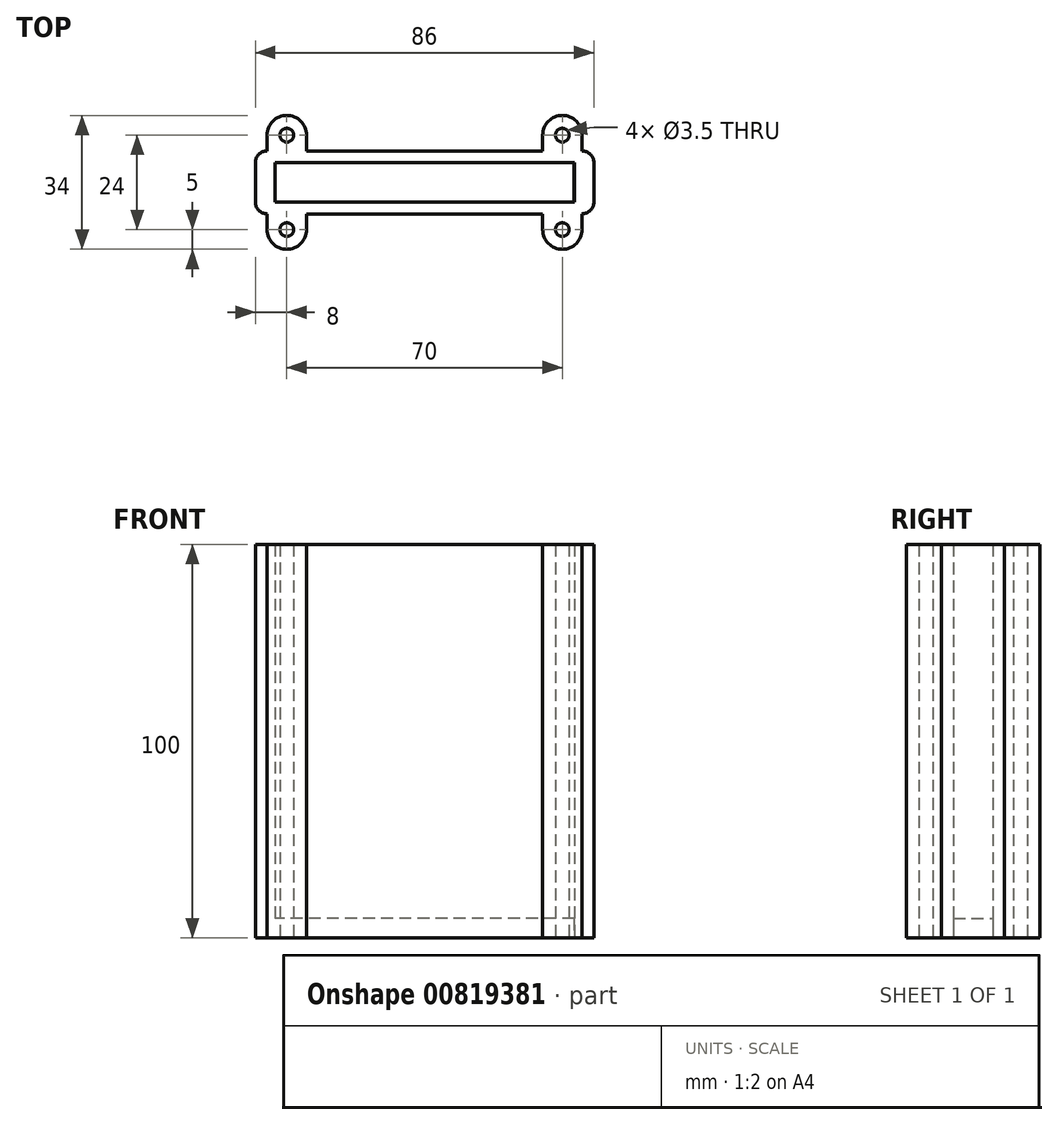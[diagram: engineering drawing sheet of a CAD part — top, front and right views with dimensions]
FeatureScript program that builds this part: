
annotation { "Feature Type Name" : "Feature", "Feature Type Description" : "" }
export const myFeature = defineFeature(function(context is Context, id is Id, definition is map)
    precondition{}
    {
        {
            var Q0;
            Q0=qCreatedBy(makeId("Top.planeOp"),FACE);
            var sketch = newSketch(context, id + "F0", { "sketchPlane" : qUnion([Q0])});
            skLineSegment(sketch, "E0.bottom", {"start": v(38.09, -5) * mm, "end": v(-37.94, -5) * mm});
            skLineSegment(sketch, "E0.top", {"start": v(38.09, 5) * mm, "end": v(-37.94, 5) * mm});
            skPoint(sketch, "E0.middle", {"position": v(0, 0) * mm});
            skLineSegment(sketch, "E1.0", {"start": v(40, 8) * mm, "end": v(-40, 8) * mm});
            skLineSegment(sketch, "E1.1", {"start": v(43, -5) * mm, "end": v(43, 5) * mm});
            skLineSegment(sketch, "E1.2", {"start": v(40, -8) * mm, "end": v(-40, -8) * mm});
            skLineSegment(sketch, "E1.3", {"start": v(-43, -5) * mm, "end": v(-43, 5) * mm});
            skPoint(sketch, "E2.visualSharp", {"position": v(-43, 8) * mm});
            skArc(sketch, "E2.filletArc", {"start": v(-40, 8) * mm, "mid": v(-42.12, 7.12) * mm, "end": v(-43, 5) * mm});
            skPoint(sketch, "E3.visualSharp", {"position": v(-43, -8) * mm});
            skArc(sketch, "E3.filletArc", {"start": v(-43, -5) * mm, "mid": v(-42.12, -7.12) * mm, "end": v(-40, -8) * mm});
            skPoint(sketch, "E4.visualSharp", {"position": v(43, 8) * mm});
            skArc(sketch, "E4.filletArc", {"start": v(43, 5) * mm, "mid": v(42.12, 7.12) * mm, "end": v(40, 8) * mm});
            skPoint(sketch, "E5.visualSharp", {"position": v(43, -8) * mm});
            skArc(sketch, "E5.filletArc", {"start": v(40, -8) * mm, "mid": v(42.12, -7.12) * mm, "end": v(43, -5) * mm});
            skLineSegment(sketch, "E6", {"start": v(40, -8) * mm, "end": v(40, -12) * mm});
            skLineSegment(sketch, "E7", {"start": v(-40, 8) * mm, "end": v(-40, 12) * mm});
            skLineSegment(sketch, "E8", {"start": v(-30, 12) * mm, "end": v(-40, 12) * mm});
            skLineSegment(sketch, "E9", {"start": v(-30, 12) * mm, "end": v(-30, 8) * mm});
            skLineSegment(sketch, "E10", {"start": v(40, 8) * mm, "end": v(40, 12) * mm});
            skLineSegment(sketch, "E11", {"start": v(40, 12) * mm, "end": v(30, 12) * mm});
            skLineSegment(sketch, "E12", {"start": v(30, 12) * mm, "end": v(30, 8) * mm});
            skArc(sketch, "E13", {"start": v(-30, 12) * mm, "mid": v(-35, 17) * mm, "end": v(-40, 12) * mm});
            skArc(sketch, "E14", {"start": v(40, 12) * mm, "mid": v(35, 17) * mm, "end": v(30, 12) * mm});
            skCircle(sketch, "E15", {"center": v(-35, 12) * mm, "radius": 1.75 * mm});
            skCircle(sketch, "E16", {"center": v(35, 12) * mm, "radius": 1.75 * mm});
            skLineSegment(sketch, "E17", {"start": v(40, -12) * mm, "end": v(30, -12) * mm});
            skLineSegment(sketch, "E18", {"start": v(30, -12) * mm, "end": v(30, -8) * mm});
            skLineSegment(sketch, "E19", {"start": v(-40, -8) * mm, "end": v(-40, -12) * mm});
            skLineSegment(sketch, "E20", {"start": v(-30, -12) * mm, "end": v(-40, -12) * mm});
            skLineSegment(sketch, "E21", {"start": v(-30, -12) * mm, "end": v(-30, -8) * mm});
            skArc(sketch, "E22", {"start": v(30, -12) * mm, "mid": v(35, -17) * mm, "end": v(40, -12) * mm});
            skArc(sketch, "E23", {"start": v(-40, -12) * mm, "mid": v(-35, -17) * mm, "end": v(-30, -12) * mm});
            skCircle(sketch, "E24", {"center": v(-35, -12) * mm, "radius": 1.75 * mm});
            skCircle(sketch, "E25", {"center": v(35, -12) * mm, "radius": 1.75 * mm});
            skLineSegment(sketch, "E26", {"start": v(-37.94, 5) * mm, "end": v(-37.94, -5) * mm});
            skLineSegment(sketch, "E27", {"start": v(38.09, 5) * mm, "end": v(38.09, -5) * mm});
            skSolve(sketch);
        }
        {
            var Q0;
            Q0=qCreatedBy(makeId("Top.planeOp"),FACE);
            var sketch = newSketch(context, id + "F1", { "sketchPlane" : qUnion([Q0])});
            skLineSegment(sketch, "E28.bottom", {"start": v(38, -5) * mm, "end": v(-38, -5) * mm});
            skLineSegment(sketch, "E28.top", {"start": v(38, 5) * mm, "end": v(-38, 5) * mm});
            skLineSegment(sketch, "E28.left", {"start": v(38, -5) * mm, "end": v(38, 5) * mm});
            skLineSegment(sketch, "E28.right", {"start": v(-38, -5) * mm, "end": v(-38, 5) * mm});
            skPoint(sketch, "E28.middle", {"position": v(0, 0) * mm});
            skSolve(sketch);
        }
        {
            var Q0;
            Q0 = qSketchRegion(id + "F1", true);
            extrude(context, id + "F2", {"entities" : qUnion([Q0]), "depth" : 5 * mm, "offsetDistance" : 25 * mm});
        }
        {
            var Q0;
            Q0 = qSketchRegion(id + "F0", true);
            extrude(context, id + "F3", {"entities" : qUnion([Q0]), "operationType" : NewBodyOperationType.ADD, "depth" : 100 * mm, "offsetDistance" : 25 * mm});
        }
    });
